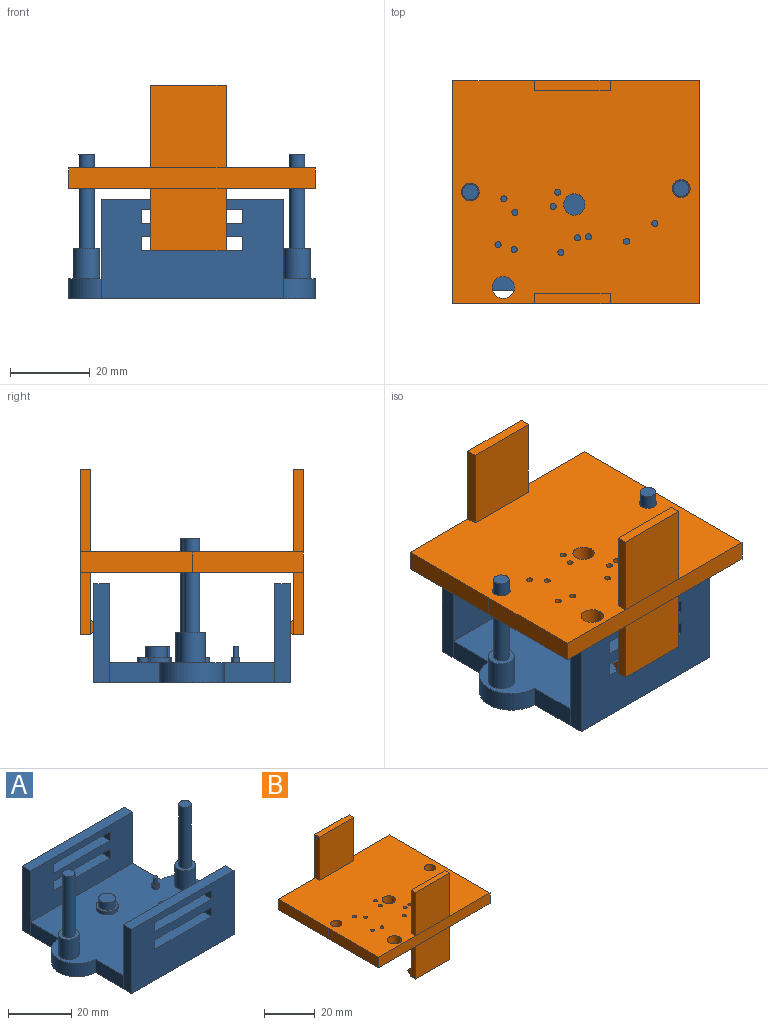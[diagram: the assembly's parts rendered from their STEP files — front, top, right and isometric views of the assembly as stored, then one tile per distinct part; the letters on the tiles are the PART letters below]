
ASSEMBLY  parts=2 mates=1
PART A: 58 faces, bbox 62x49.3x36.3 mm
  f0: plane 12.68x5.08mm, normal (1,0,0), area 64.4mm2, adj f1,f6,f7,f32
  f1: plane 61.98x41.64mm, normal (0,0,1), area 1985mm2, adj f0,f2,f3,f4,f5,f6,f8,f10
  f2: plane 12.72x5.1mm, normal (-1,0,0), area 64.5mm2, adj f1,f3,f7,f33
  f3: cylinder r=8.13mm len=16.26mm, axis (0,0,-1), area 129.7mm2, adj f1,f2,f4,f7
  f4: plane 12.69x5.08mm, normal (-1,0,0), area 64.4mm2, adj f1,f3,f7,f38
  f5: plane 12.68x5.08mm, normal (1,0,0), area 64.4mm2, adj f1,f6,f7,f37
  f6: cylinder r=8.13mm len=16.26mm, axis (0,0,-1), area 129.7mm2, adj f0,f1,f5,f7
  f7: plane 61.98x49.32mm, normal (0,0,-1), area 2462.4mm2, adj f0,f2,f3,f4,f5,f6,f32,f33
  f8: cylinder r=3.48mm len=6.96mm, axis (0,0,-1), area 27.8mm2, adj f1,f9
  f9: plane 6.96x6.96mm, normal (0,0,1), area 15.7mm2, adj f8,f18
  f10: cylinder r=1.37mm len=2.74mm, axis (0,0,-1), area 10.9mm2, adj f1,f11
  f11: plane 2.74x2.74mm, normal (0,0,1), area 5.9mm2, adj f10
  f12: cylinder r=1.37mm len=2.74mm, axis (0,0,-1), area 10.9mm2, adj f1,f13
  f13: plane 2.74x2.74mm, normal (0,0,1), area 5.9mm2, adj f12
  f14: cylinder r=1.14mm len=2.29mm, axis (0,0,-1), area 9.1mm2, adj f1,f15
  f15: plane 2.29x2.29mm, normal (0,0,1), area 2.6mm2, adj f14,f19
  f16: cylinder r=1.01mm len=2.02mm, axis (0,0,-1), area 8.1mm2, adj f1,f17
  f17: plane 2.02x2.02mm, normal (0,0,1), area 1.8mm2, adj f16,f20
  f18: cylinder r=2.67mm len=5.34mm, axis (0,0,-1), area 46.9mm2, adj f9,f21
  f19: cylinder r=0.7mm len=2.79mm, axis (0,0,-1), area 12.3mm2, adj f15,f22
  f20: cylinder r=0.66mm len=2.79mm, axis (0,0,-1), area 11.5mm2, adj f17,f23
  f21: plane 5.34x5.34mm, normal (0,0,1), area 22.4mm2, adj f18
  f22: plane 1.4x1.4mm, normal (0,0,1), area 1.5mm2, adj f19
  f23: plane 1.31x1.31mm, normal (0,0,1), area 1.4mm2, adj f20
  f24: plane 6.59x6.59mm, normal (0,0,1), area 21.9mm2, adj f25,f30
  f25: cylinder r=3.29mm len=7.62mm, axis (0,0,-1), area 157.7mm2, adj f1,f24
  f26: plane 6.59x6.59mm, normal (0,0,1), area 21.9mm2, adj f27,f28
  f27: cylinder r=3.29mm len=7.62mm, axis (0,0,-1), area 157.7mm2, adj f1,f26
  f28: cylinder r=1.97mm len=23.62mm, axis (0,0,-1), area 292.2mm2, adj f26,f29
  f29: plane 3.94x3.94mm, normal (0,0,1), area 12.2mm2, adj f28
  f30: cylinder r=1.97mm len=23.62mm, axis (0,0,-1), area 292.2mm2, adj f24,f31
  f31: plane 3.94x3.94mm, normal (0,0,1), area 12.2mm2, adj f30
  f32: plane 45.74x24.89mm, normal (0,-1,0), area 725.2mm2, adj f0,f1,f7,f33,f34,f36,f50,f51
  f33: plane 24.91x3.87mm, normal (-1,0,0), area 95.7mm2, adj f2,f7,f32,f35,f36
  f34: plane 24.89x3.85mm, normal (1,0,0), area 95.7mm2, adj f7,f32,f35,f36
  f35: plane 45.74x24.89mm, normal (0,1,0), area 957.5mm2, adj f7,f33,f34,f36,f50,f51,f52,f53
  f36: plane 45.74x3.85mm, normal (0,0,1), area 175.9mm2, adj f32,f33,f34,f35
  f37: plane 45.74x24.89mm, normal (0,1,0), area 725.2mm2, adj f1,f5,f7,f38,f40,f41,f42,f43
  f38: plane 24.89x3.85mm, normal (-1,0,0), area 95.7mm2, adj f4,f7,f37,f39,f41
  f39: plane 45.74x24.89mm, normal (0,-1,0), area 957.5mm2, adj f7,f38,f40,f41,f42,f43,f44,f45
  f40: plane 24.89x3.85mm, normal (1,0,0), area 95.7mm2, adj f7,f37,f39,f41
  f41: plane 45.74x3.85mm, normal (0,0,1), area 175.9mm2, adj f37,f38,f39,f40
  f42: plane 3.85x3.56mm, normal (-1,0,0), area 13.7mm2, adj f37,f39,f43,f45
  f43: plane 25.41x3.85mm, normal (0,0,1), area 97.7mm2, adj f37,f39,f42,f44
  f44: plane 3.85x3.56mm, normal (1,0,0), area 13.7mm2, adj f37,f39,f43,f45
  f45: plane 25.41x3.85mm, normal (0,0,-1), area 97.7mm2, adj f37,f39,f42,f44
  f46: plane 3.85x3.56mm, normal (-1,0,0), area 13.7mm2, adj f37,f39,f47,f49
  f47: plane 25.41x3.85mm, normal (0,0,1), area 97.7mm2, adj f37,f39,f46,f48
  f48: plane 3.85x3.56mm, normal (1,0,0), area 13.7mm2, adj f37,f39,f47,f49
  f49: plane 25.41x3.85mm, normal (0,0,-1), area 97.7mm2, adj f37,f39,f46,f48
  f50: plane 25.41x3.85mm, normal (0,0,-1), area 97.7mm2, adj f32,f35,f51,f53
  f51: plane 3.85x3.56mm, normal (1,0,0), area 13.7mm2, adj f32,f35,f50,f52
  f52: plane 25.41x3.85mm, normal (0,0,1), area 97.7mm2, adj f32,f35,f51,f53
  f53: plane 3.85x3.56mm, normal (-1,0,0), area 13.7mm2, adj f32,f35,f50,f52
  f54: plane 25.41x3.85mm, normal (0,0,-1), area 97.7mm2, adj f32,f35,f55,f57
  f55: plane 3.85x3.56mm, normal (1,0,0), area 13.7mm2, adj f32,f35,f54,f56
  f56: plane 25.41x3.85mm, normal (0,0,1), area 97.7mm2, adj f32,f35,f55,f57
  f57: plane 3.85x3.56mm, normal (-1,0,0), area 13.7mm2, adj f32,f35,f54,f56
PART B: 50 faces, bbox 62x56x41.7 mm
  f0: plane 22.46x5.08mm, normal (0,1,0), area 114.1mm2, adj f1,f2,f5,f25
  f1: plane 62.03x55.98mm, normal (0,0,1), area 3277.5mm2, adj f0,f3,f4,f5,f6,f7,f8,f9
  f2: plane 62.03x55.98mm, normal (0,0,-1), area 3277.5mm2, adj f0,f3,f4,f5,f6,f7,f8,f9
  f3: plane 28x5.08mm, normal (-1,0,0), area 142.2mm2, adj f1,f2,f4,f21
  f4: plane 62.04x5.09mm, normal (0,-1,0), area 315.1mm2, adj f1,f2,f3,f5,f34,f35
  f5: plane 55.98x5.08mm, normal (1,0,0), area 284.4mm2, adj f0,f1,f2,f4
  f6: plane 20.6x5.08mm, normal (0,1,0), area 104.6mm2, adj f1,f2,f21,f27
  f7: cylinder r=0.76mm len=5.08mm, axis (0,0,-1), area 24.3mm2, adj f1,f2
  f8: cylinder r=0.76mm len=5.08mm, axis (0,0,-1), area 24.3mm2, adj f1,f2
  f9: cylinder r=0.76mm len=5.08mm, axis (0,0,-1), area 24.3mm2, adj f1,f2
  f10: cylinder r=0.76mm len=5.08mm, axis (0,0,-1), area 24.3mm2, adj f1,f2
  f11: cylinder r=0.76mm len=5.08mm, axis (0,0,-1), area 24.3mm2, adj f1,f2
  f12: cylinder r=0.76mm len=5.08mm, axis (0,0,-1), area 24.3mm2, adj f1,f2
  f13: cylinder r=0.76mm len=5.08mm, axis (0,0,-1), area 24.3mm2, adj f1,f2
  f14: cylinder r=0.76mm len=5.08mm, axis (0,0,-1), area 24.3mm2, adj f1,f2
  f15: cylinder r=0.76mm len=5.08mm, axis (0,0,-1), area 24.3mm2, adj f1,f2
  f16: cylinder r=0.76mm len=5.08mm, axis (0,0,-1), area 24.3mm2, adj f1,f2
  f17: cylinder r=2.22mm len=5.08mm, axis (0,0,-1), area 70.9mm2, adj f1,f2
  f18: cylinder r=2.22mm len=5.08mm, axis (0,0,-1), area 70.9mm2, adj f1,f2
  f19: cylinder r=2.78mm len=5.55mm, axis (0,0,-1), area 88.6mm2, adj f1,f2
  f20: cylinder r=0.76mm len=5.08mm, axis (0,0,-1), area 24.3mm2, adj f1,f2
  f21: plane 27.99x5.08mm, normal (-1,0,0), area 142.2mm2, adj f1,f2,f3,f6
  f22: cylinder r=2.67mm len=5.34mm, axis (0,0,-1), area 85.3mm2, adj f1,f2
  f23: plane 18.94x15.75mm, normal (0,-1,0), area 227.2mm2, adj f2,f25,f27,f28,f45,f47,f48,f49
  f24: plane 20.83x18.94mm, normal (0,-1,0), area 394.6mm2, adj f1,f25,f27,f29
  f25: plane 41.66x2.54mm, normal (1,0,0), area 93.2mm2, adj f0,f1,f2,f23,f24,f26,f28,f29
  f26: plane 41.66x18.94mm, normal (0,1,0), area 789.1mm2, adj f25,f27,f28,f29
  f27: plane 41.66x2.54mm, normal (-1,0,0), area 93.2mm2, adj f1,f2,f6,f23,f24,f26,f28,f29
  f28: plane 18.94x2.54mm, normal (0,0,-1), area 48.2mm2, adj f23,f25,f26,f27
  f29: plane 18.94x2.54mm, normal (0,0,1), area 48.2mm2, adj f24,f25,f26,f27
  f30: plane 18.96x2.54mm, normal (0,0,-1), area 48.2mm2, adj f31,f32,f33,f34
  f31: plane 15.75x2.54mm, normal (-1,0,0), area 40.1mm2, adj f2,f30,f32,f34
  f32: plane 18.96x15.75mm, normal (0,1,0), area 227.4mm2, adj f2,f30,f31,f33,f40,f41,f42,f43
  f33: plane 15.75x2.54mm, normal (1,0,0), area 40.1mm2, adj f2,f30,f32,f34
  f34: plane 18.96x15.75mm, normal (0,-1,0), area 298.5mm2, adj f4,f30,f31,f33
  f35: plane 20.83x18.96mm, normal (0,-1,0), area 394.8mm2, adj f4,f36,f38,f39
  f36: plane 20.83x2.54mm, normal (1,0,0), area 53mm2, adj f1,f35,f37,f39
  f37: plane 20.83x18.96mm, normal (0,1,0), area 394.8mm2, adj f1,f36,f38,f39
  f38: plane 20.83x2.54mm, normal (-1,0,0), area 53mm2, adj f1,f35,f37,f39
  f39: plane 18.96x2.54mm, normal (0,0,1), area 48.2mm2, adj f35,f36,f37,f38
  f40: plane 18.8x2mm, normal (0,0.71,0.71), area 53.1mm2, adj f32,f42,f43,f44
  f41: plane 18.8x0.11mm, normal (0,-0.71,-0.71), area 2.8mm2, adj f32,f42,f43,f44
  f42: plane 3.89x2mm, normal (1,0,0), area 4mm2, adj f32,f40,f41,f44
  f43: plane 3.89x2mm, normal (-1,0,0), area 4mm2, adj f32,f40,f41,f44
  f44: plane 18.8x1.89mm, normal (0,0.71,-0.71), area 50.3mm2, adj f40,f41,f42,f43
  f45: plane 18.8x1.9mm, normal (0,-0.71,0.71), area 50.6mm2, adj f23,f46,f48,f49
  f46: plane 18.8x1.89mm, normal (0,-0.71,-0.71), area 50.3mm2, adj f45,f47,f48,f49
  f47: plane 18.8x0.01mm, normal (0,0.71,-0.71), area 0.3mm2, adj f23,f46,f48,f49
  f48: plane 3.8x1.9mm, normal (1,0,0), area 3.6mm2, adj f23,f45,f46,f47
  f49: plane 3.8x1.9mm, normal (-1,0,0), area 3.6mm2, adj f23,f45,f46,f47
PLACE A t=(-14.5,-61.74,-58.78)mm
PLACE B t=(-15.8,-73.29,-30.97)mm
MATE slider A.f30 <-> B.f18  axis (0,0,-1) through (-41.43,-58.21,-34.27)mm
